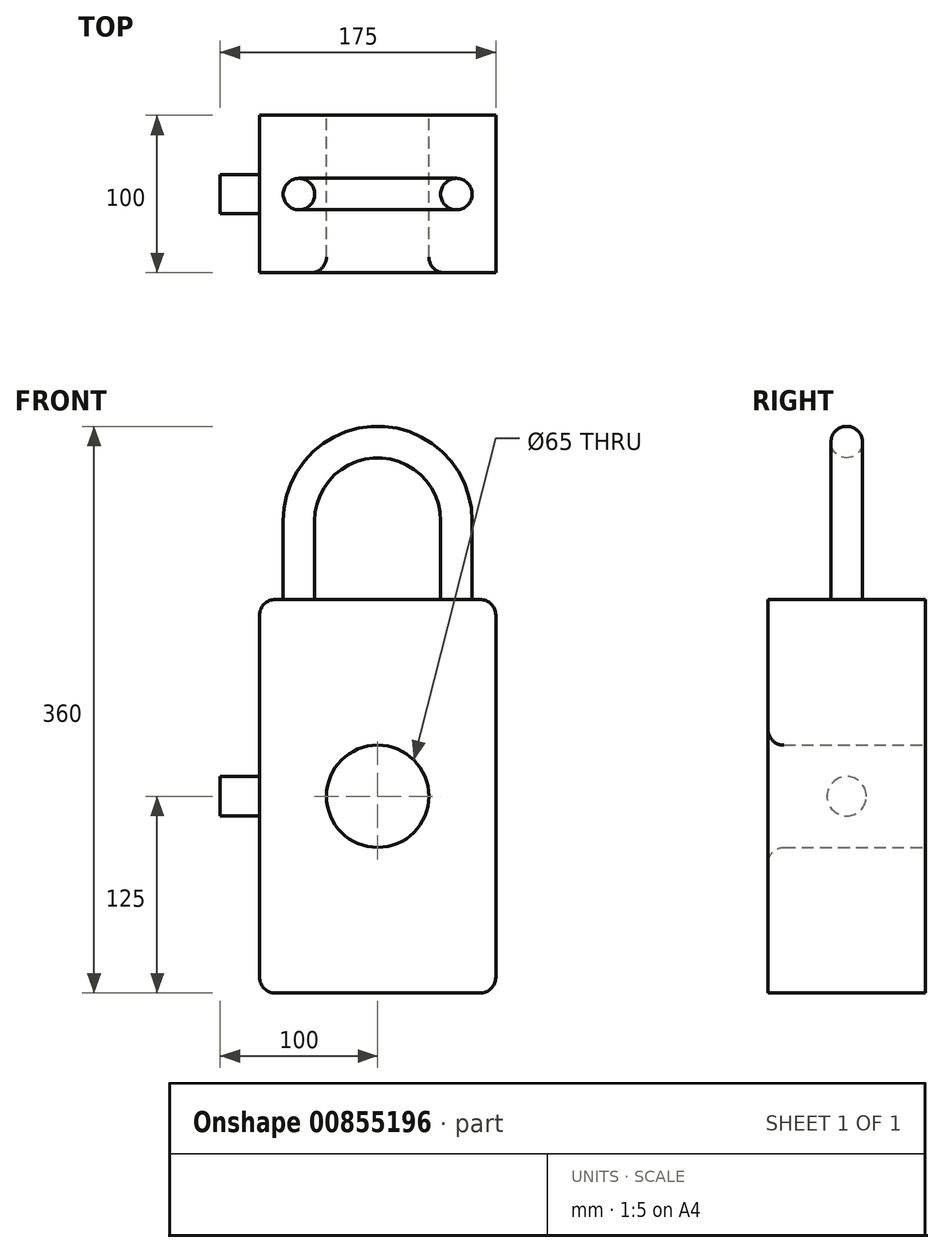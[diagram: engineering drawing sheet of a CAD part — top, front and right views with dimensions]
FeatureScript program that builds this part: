
annotation { "Feature Type Name" : "Feature", "Feature Type Description" : "" }
export const myFeature = defineFeature(function(context is Context, id is Id, definition is map)
    precondition{}
    {
        {
            var Q0;
            Q0=qCreatedBy(makeId("Top.planeOp"),FACE);
            var sketch = newSketch(context, id + "F0", { "sketchPlane" : qUnion([Q0])});
            skPoint(sketch, "E0.middle", {"position": v(0, 0) * mm});
            skLineSegment(sketch, "E1.bottom", {"start": v(75, 50) * mm, "end": v(-75, 50) * mm});
            skLineSegment(sketch, "E1.top", {"start": v(75, -50) * mm, "end": v(-75, -50) * mm});
            skLineSegment(sketch, "E1.left", {"start": v(75, 50) * mm, "end": v(75, -50) * mm});
            skLineSegment(sketch, "E1.right", {"start": v(-75, 50) * mm, "end": v(-75, -50) * mm});
            skSolve(sketch);
        }
        {
            var Q0;
            Q0 = qSketchRegion(id + "F0", true);
            extrude(context, id + "F1", {"entities" : qUnion([Q0]), "depth" : 250 * mm, "offsetDistance" : 25 * mm});
        }
        {
            var Q0;
            Q0=makeQuery(id+"F1.opExtrude","SWEPT_FACE",FACE,{"disambiguationData":[OSD([sQuery(id+"F0.wireOp",EDGE,"E1.bottom")])]});
            var sketch = newSketch(context, id + "F2", { "sketchPlane" : qUnion([Q0])});
            skCircle(sketch, "E2", {"center": v(0, 125) * mm, "radius": 32.5 * mm});
            skSolve(sketch);
        }
        {
            var Q0;
            Q0 = qSketchRegion(id + "F2", true);
            extrude(context, id + "F3", {"entities" : qUnion([Q0]), "operationType" : NewBodyOperationType.REMOVE, "endBound" : BoundingType.THROUGH_ALL, "oppositeDirection" : true, "depth" : 25 * mm, "offsetDistance" : 25 * mm});
        }
        {
            var Q0;
            Q0=makeQuery(id+"F1.opExtrude","CAP_EDGE",EDGE,{"disambiguationData":[OSD([sQuery(id+"F0.wireOp",EDGE,"E1.right")])],"isStart":false});
            var Q1;
            Q1=makeQuery(id+"F1.opExtrude","CAP_EDGE",EDGE,{"disambiguationData":[OSD([sQuery(id+"F0.wireOp",EDGE,"E1.left")])],"isStart":false});
            var Q2;
            Q2=makeQuery(id+"F1.opExtrude","CAP_EDGE",EDGE,{"disambiguationData":[OSD([sQuery(id+"F0.wireOp",EDGE,"E1.left")])],"isStart":true});
            var Q3;
            Q3=makeQuery(id+"F1.opExtrude","CAP_EDGE",EDGE,{"disambiguationData":[OSD([sQuery(id+"F0.wireOp",EDGE,"E1.right")])],"isStart":true});
            var Q4;
            Q4=makeQuery(id+"F3.boolean.opBoolean","INTERSECT",EDGE,{"derivedFrom":[makeQuery(id+"F1.opExtrude","SWEPT_FACE",FACE,{"disambiguationData":[OSD([sQuery(id+"F0.wireOp",EDGE,"E1.top")])]}),makeQuery(id+"F3.opExtrude","SWEPT_FACE",FACE,{"disambiguationData":[OSD([sQuery(id+"F2.wireOp",EDGE,"E2")])]})]});
            var Q5;
            Q5=makeQuery(id+"F3.boolean.opBoolean","COPY",EDGE,{"derivedFrom":makeQuery(id+"F3.opExtrude","CAP_EDGE",EDGE,{"disambiguationData":[OSD([sQuery(id+"F2.wireOp",EDGE,"E2")])],"isStart":true})});
            fillet(context, id + "F4", {"entities" : qUnion([Q0, Q1, Q2, Q3, Q4, Q5]), "radius" : 10 * mm, "tangentPropagation" : true, "allowEdgeOverflow" : false});
        }
        {
            var Q0;
            Q0=makeQuery(id+"F1.opExtrude","SWEPT_FACE",FACE,{"disambiguationData":[OSD([sQuery(id+"F0.wireOp",EDGE,"E1.right")])]});
            var sketch = newSketch(context, id + "F5", { "sketchPlane" : qUnion([Q0])});
            skCircle(sketch, "E3", {"center": v(0, 125) * mm, "radius": 12.5 * mm});
            skPoint(sketch, "E3.centerSnap0", {"position": v(-50, 125) * mm});
            skPoint(sketch, "E3.centerSnap1", {"position": v(0, 240) * mm});
            skSolve(sketch);
        }
        {
            var Q0;
            Q0 = qSketchRegion(id + "F5", true);
            extrude(context, id + "F6", {"entities" : qUnion([Q0]), "operationType" : NewBodyOperationType.ADD, "depth" : 25 * mm, "offsetDistance" : 25 * mm});
        }
        {
            var Q0;
            Q0=makeQuery(id+"F1.opExtrude","CAP_FACE",FACE,{"disambiguationData":[OSD([sQuery(id+"F0.wireOp",EDGE,"E1.bottom"),sQuery(id+"F0.wireOp",EDGE,"E1.top"),sQuery(id+"F0.wireOp",EDGE,"E1.left"),sQuery(id+"F0.wireOp",EDGE,"E1.right")])],"isStart":false});
            var sketch = newSketch(context, id + "F7", { "sketchPlane" : qUnion([Q0])});
            skLineSegment(sketch, "E4", {"start": v(-50, 0) * mm, "end": v(50, 0) * mm, "construction": true});
            skCircle(sketch, "E5", {"center": v(50, 0) * mm, "radius": 10 * mm});
            skSolve(sketch);
        }
        {
            var Q0;
            Q0=qCreatedBy(makeId("Front.planeOp"),FACE);
            var sketch = newSketch(context, id + "F8", { "sketchPlane" : qUnion([Q0])});
            skLineSegment(sketch, "E6", {"start": v(-50, 250) * mm, "end": v(-50, 300) * mm});
            skLineSegment(sketch, "E7", {"start": v(50, 250) * mm, "end": v(50, 300) * mm});
            skArc(sketch, "E8", {"start": v(50, 300) * mm, "mid": v(0, 350) * mm, "end": v(-50, 300) * mm});
            skSolve(sketch);
        }
        {
            var Q0;
            Q0 = qSketchRegion(id + "F7", true);
            var Q1;
            Q1 = qConstructionFilter(qBodyType(qCreatedBy(id + "F8" ,EDGE), BodyType.WIRE), ConstructionObject.NO);
            sweep(context, id + "F9", {"operationType" : NewBodyOperationType.ADD, "profiles" : qUnion([Q0]), "path" : qUnion([Q1])});
        }
    });
